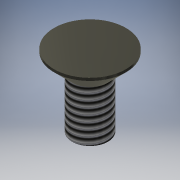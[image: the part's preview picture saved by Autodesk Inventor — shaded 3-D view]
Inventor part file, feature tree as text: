
AUTODESK INVENTOR PART (.ipt)
format: ipt  version: 2016 (Build 200138000, 138)  size: 125,952 bytes
history: native  units: mm
features: extrude x3, sketch x3, other x1, thread x1, chamfer x1
ambient origin geometry x1: Origin
bodies: Body1 (feature_tree)
feature tree (9):
  other  "ソリッド1"
  extrude  "押し出し1"  Depth=4.0mm
  extrude  "押し出し2"  Depth=6.0mm TaperAngle=0.0deg
  thread  "ねじ1"
  extrude  "押し出し3"  Depth=8.0mm
  chamfer  "面取り1"  Distance=2.3mm
  sketch  "スケッチ1"
  sketch  "スケッチ2"
  sketch  "スケッチ3"
